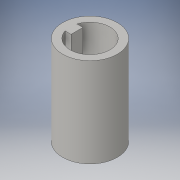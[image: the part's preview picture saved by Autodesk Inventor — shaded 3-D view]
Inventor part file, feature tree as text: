
AUTODESK INVENTOR PART (.ipt)
format: ipt  version: 2016 (Build 200138000, 138)  size: 98,304 bytes
history: native  units: in
note: dims shown in document units (in); Inventor stores cm internally (conversion verified against a paired STEP export)
features: extrude x1, sketch x1
ambient origin geometry x8: Origin, YZ Plane, XZ Plane, XY Plane, X Axis, Y Axis, Z Axis, Center Point
bodies: Solid1 (feature_tree)
feature tree (2):
  extrude  "Extrusion1"  Depth=1.5in
  sketch  "Sketch1"  dims[d0=0.918in d1=0.668in d3=0.2in d4=0.1in d5=1.5in d6=0.0in]
